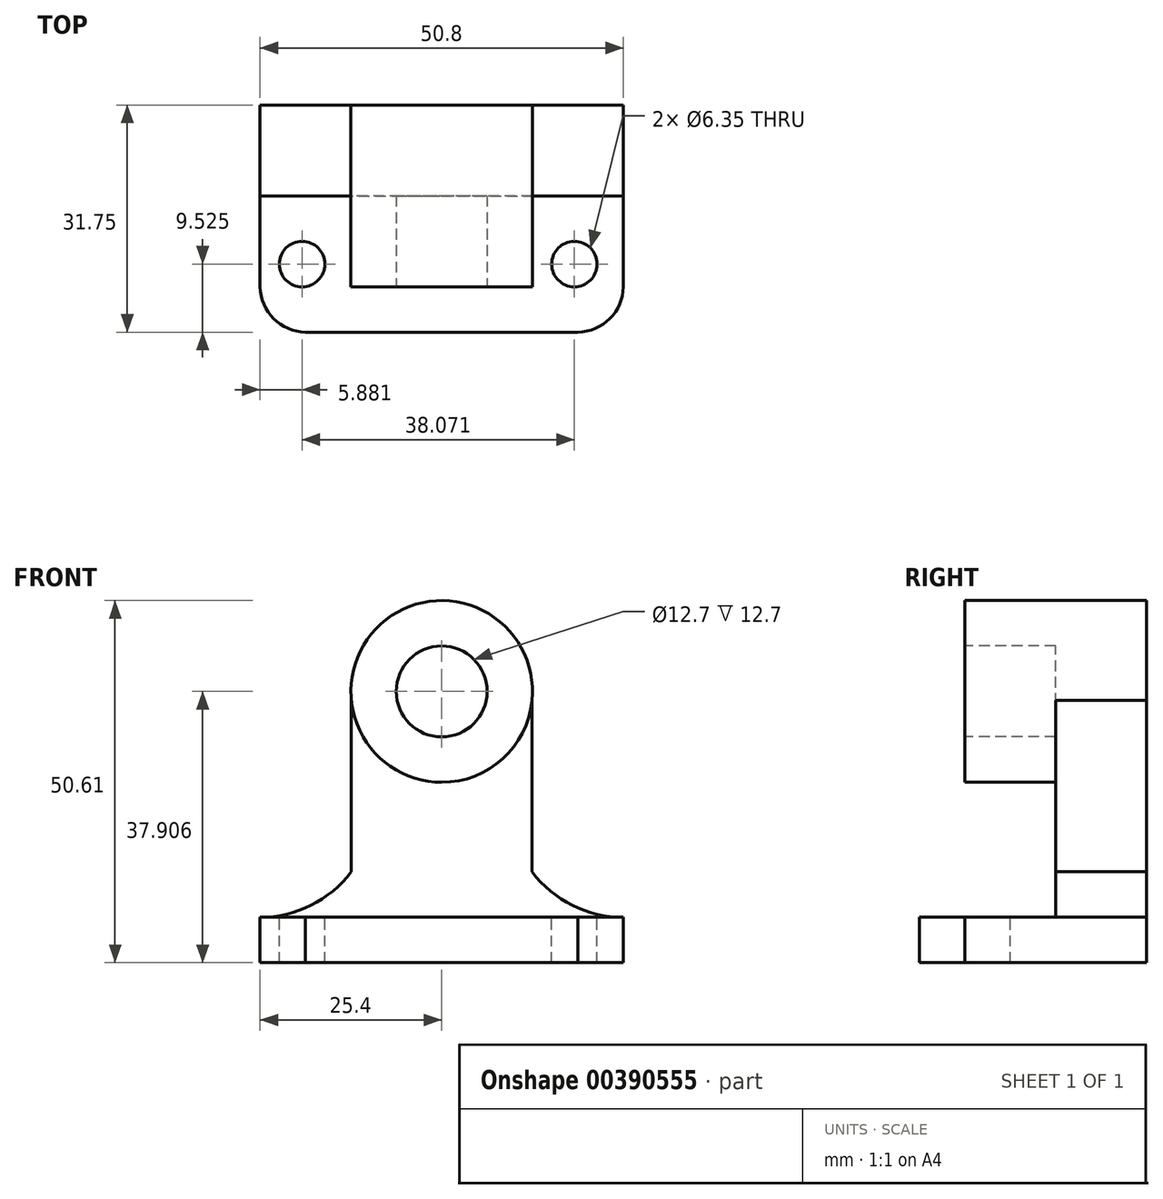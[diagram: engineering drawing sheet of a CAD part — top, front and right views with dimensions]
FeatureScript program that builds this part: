
annotation { "Feature Type Name" : "Feature", "Feature Type Description" : "" }
export const myFeature = defineFeature(function(context is Context, id is Id, definition is map)
    precondition{}
    {
        {
            var Q0;
            Q0=qCreatedBy(makeId("Top.planeOp"),FACE);
            var sketch = newSketch(context, id + "F0", { "sketchPlane" : qUnion([Q0])});
            skLineSegment(sketch, "E0", {"start": v(0, 0) * mm, "end": v(50.8, 0) * mm});
            skLineSegment(sketch, "E1", {"start": v(50.8, 0) * mm, "end": v(50.8, 31.75) * mm});
            skLineSegment(sketch, "E2", {"start": v(50.8, 31.75) * mm, "end": v(0, 31.75) * mm});
            skLineSegment(sketch, "E3", {"start": v(0, 31.75) * mm, "end": v(0, 0) * mm});
            skSolve(sketch);
        }
        {
            var Q0;
            Q0 = qSketchRegion(id + "F0", true);
            extrude(context, id + "F1", {"entities" : qUnion([Q0]), "depth" : 6.35 * mm});
        }
        {
            var Q0;
            Q0=makeQuery(id+"F1.opExtrude","CAP_FACE",FACE,{"disambiguationData":[OSD([sQuery(id+"F0.wireOp",EDGE,"E0"),sQuery(id+"F0.wireOp",EDGE,"E1"),sQuery(id+"F0.wireOp",EDGE,"E2"),sQuery(id+"F0.wireOp",EDGE,"E3")])],"isStart":false});
            var sketch = newSketch(context, id + "F2", { "sketchPlane" : qUnion([Q0])});
            skLineSegment(sketch, "E4", {"start": v(0, 19.05) * mm, "end": v(50.8, 19.05) * mm});
            skSolve(sketch);
        }
        {
            var Q0;
            Q0 = qSketchRegion(id + "F2", true);
            var Q1;
            {var subQ0=sQuery(id+"F2.wireOp",EDGE,"E4");Q1=makeQuery(id+"F2.imprint","IMPRINT",FACE,{"disambiguationData":[TD([[makeQuery(id+"F2.imprint","IMPRINT",EDGE,{"derivedFrom":subQ0}),1.0]])]});}
            extrude(context, id + "F3", {"entities" : qUnion([Q0, Q1]), "operationType" : NewBodyOperationType.ADD, "depth" : 44.45 * mm});
        }
        {
            var Q0;
            Q0=makeQuery(id+"F3.opExtrude","SWEPT_FACE",FACE,{"disambiguationData":[OSD([sQuery(id+"F2.wireOp",EDGE,"E4")])]});
            var sketch = newSketch(context, id + "F4", { "sketchPlane" : qUnion([Q0])});
            skCircle(sketch, "E5", {"center": v(25.4, 37.9) * mm, "radius": 12.7 * mm});
            skPoint(sketch, "E5.centerSnap0", {"position": v(25.4, 50.8) * mm});
            skSolve(sketch);
        }
        {
            var Q0;
            Q0 = qSketchRegion(id + "F4", true);
            extrude(context, id + "F5", {"entities" : qUnion([Q0]), "operationType" : NewBodyOperationType.ADD, "depth" : 12.7 * mm});
        }
        {
            var Q0;
            Q0=makeQuery(id+"F5.opExtrude","CAP_FACE",FACE,{"disambiguationData":[OSD([sQuery(id+"F4.wireOp",EDGE,"E5")])],"isStart":false});
            var sketch = newSketch(context, id + "F6", { "sketchPlane" : qUnion([Q0])});
            skCircle(sketch, "E6", {"center": v(25.4, 37.9) * mm, "radius": 6.35 * mm});
            skSolve(sketch);
        }
        {
            var Q0;
            Q0=makeQuery(id+"F6.imprint","IMPRINT",FACE,{"disambiguationData":[TD([[makeQuery(id+"F6.imprint","IMPRINT",EDGE,{"derivedFrom":sQuery(id+"F6.wireOp",EDGE,"E6")}),1.0]])]});
            extrude(context, id + "F7", {"entities" : qUnion([Q0]), "operationType" : NewBodyOperationType.REMOVE, "oppositeDirection" : true, "depth" : 12.7 * mm});
        }
        {
            var Q0;
            Q0=makeQuery(id+"F1.opExtrude","CAP_FACE",FACE,{"disambiguationData":[OSD([sQuery(id+"F0.wireOp",EDGE,"E0"),sQuery(id+"F0.wireOp",EDGE,"E1"),sQuery(id+"F0.wireOp",EDGE,"E2"),sQuery(id+"F0.wireOp",EDGE,"E3")])],"isStart":false});
            var sketch = newSketch(context, id + "F8", { "sketchPlane" : qUnion([Q0])});
            skCircle(sketch, "E7", {"center": v(5.88, 9.52) * mm, "radius": 3.18 * mm});
            skPoint(sketch, "E7.centerSnap0", {"position": v(0, 9.52) * mm});
            skCircle(sketch, "E8", {"center": v(43.95, 9.52) * mm, "radius": 3.18 * mm});
            skSolve(sketch);
        }
        {
            var Q0;
            Q0=makeQuery(id+"F8.imprint","IMPRINT",FACE,{"disambiguationData":[TD([[makeQuery(id+"F8.imprint","IMPRINT",EDGE,{"derivedFrom":sQuery(id+"F8.wireOp",EDGE,"E7")}),1.0]])]});
            var Q1;
            Q1=makeQuery(id+"F8.imprint","IMPRINT",FACE,{"disambiguationData":[TD([[makeQuery(id+"F8.imprint","IMPRINT",EDGE,{"derivedFrom":sQuery(id+"F8.wireOp",EDGE,"E8")}),1.0]])]});
            extrude(context, id + "F9", {"entities" : qUnion([Q0, Q1]), "operationType" : NewBodyOperationType.REMOVE, "oppositeDirection" : true, "depth" : 25.4 * mm});
        }
        {
            var Q0;
            Q0=makeQuery(id+"F1.opExtrude","CAP_FACE",FACE,{"disambiguationData":[OSD([sQuery(id+"F0.wireOp",EDGE,"E0"),sQuery(id+"F0.wireOp",EDGE,"E1"),sQuery(id+"F0.wireOp",EDGE,"E2"),sQuery(id+"F0.wireOp",EDGE,"E3")])],"isStart":false});
            var sketch = newSketch(context, id + "F10", { "sketchPlane" : qUnion([Q0])});
            skArc(sketch, "E9", {"start": v(0, 6.35) * mm, "mid": v(1.9, 1.9) * mm, "end": v(6.35, 0) * mm});
            skArc(sketch, "E10", {"start": v(44.45, 0) * mm, "mid": v(48.9, 1.9) * mm, "end": v(50.8, 6.35) * mm});
            skSolve(sketch);
        }
        {
            var Q0;
            {var subQ0=sQuery(id+"F10.wireOp",EDGE,"E10");Q0=makeQuery(id+"F10.imprint","IMPRINT",FACE,{"disambiguationData":[TD([[makeQuery(id+"F10.imprint","IMPRINT",EDGE,{"derivedFrom":subQ0}),-1.0]])]});}
            var Q1;
            {var subQ0=sQuery(id+"F10.wireOp",EDGE,"E9");Q1=makeQuery(id+"F10.imprint","IMPRINT",FACE,{"disambiguationData":[TD([[makeQuery(id+"F10.imprint","IMPRINT",EDGE,{"derivedFrom":subQ0}),-1.0]])]});}
            extrude(context, id + "F11", {"entities" : qUnion([Q0, Q1]), "operationType" : NewBodyOperationType.REMOVE, "oppositeDirection" : true, "depth" : 25.4 * mm});
        }
        {
            var Q0;
            Q0=makeQuery(id+"F3.opExtrude","SWEPT_FACE",FACE,{"disambiguationData":[OSD([sQuery(id+"F2.wireOp",EDGE,"E4")])]});
            var sketch = newSketch(context, id + "F12", { "sketchPlane" : qUnion([Q0])});
            skLineSegment(sketch, "E11", {"start": v(38.04, 36.64) * mm, "end": v(38.04, 12.7) * mm});
            skLineSegment(sketch, "E12", {"start": v(12.76, 36.64) * mm, "end": v(12.76, 12.7) * mm});
            skArc(sketch, "E13", {"start": v(38.04, 12.7) * mm, "mid": v(43.67, 8.03) * mm, "end": v(50.8, 6.35) * mm});
            skArc(sketch, "E14", {"start": v(0, 6.35) * mm, "mid": v(7.13, 8.03) * mm, "end": v(12.76, 12.7) * mm});
            skSolve(sketch);
        }
        {
            var Q0;
            Q0 = qSketchRegion(id + "F12", true);
            var Q1;
            {var subQ1=sQuery(id+"F12.wireOp",EDGE,"E11");Q1=makeQuery(id+"F12.imprint","IMPRINT",FACE,{"disambiguationData":[TD([[makeQuery(id+"F12.imprint","IMPRINT",EDGE,{"derivedFrom":subQ1}),1.0]])]});}
            extrude(context, id + "F13", {"entities" : qUnion([Q0, Q1]), "operationType" : NewBodyOperationType.REMOVE, "oppositeDirection" : true, "depth" : 25.4 * mm});
        }
    });
